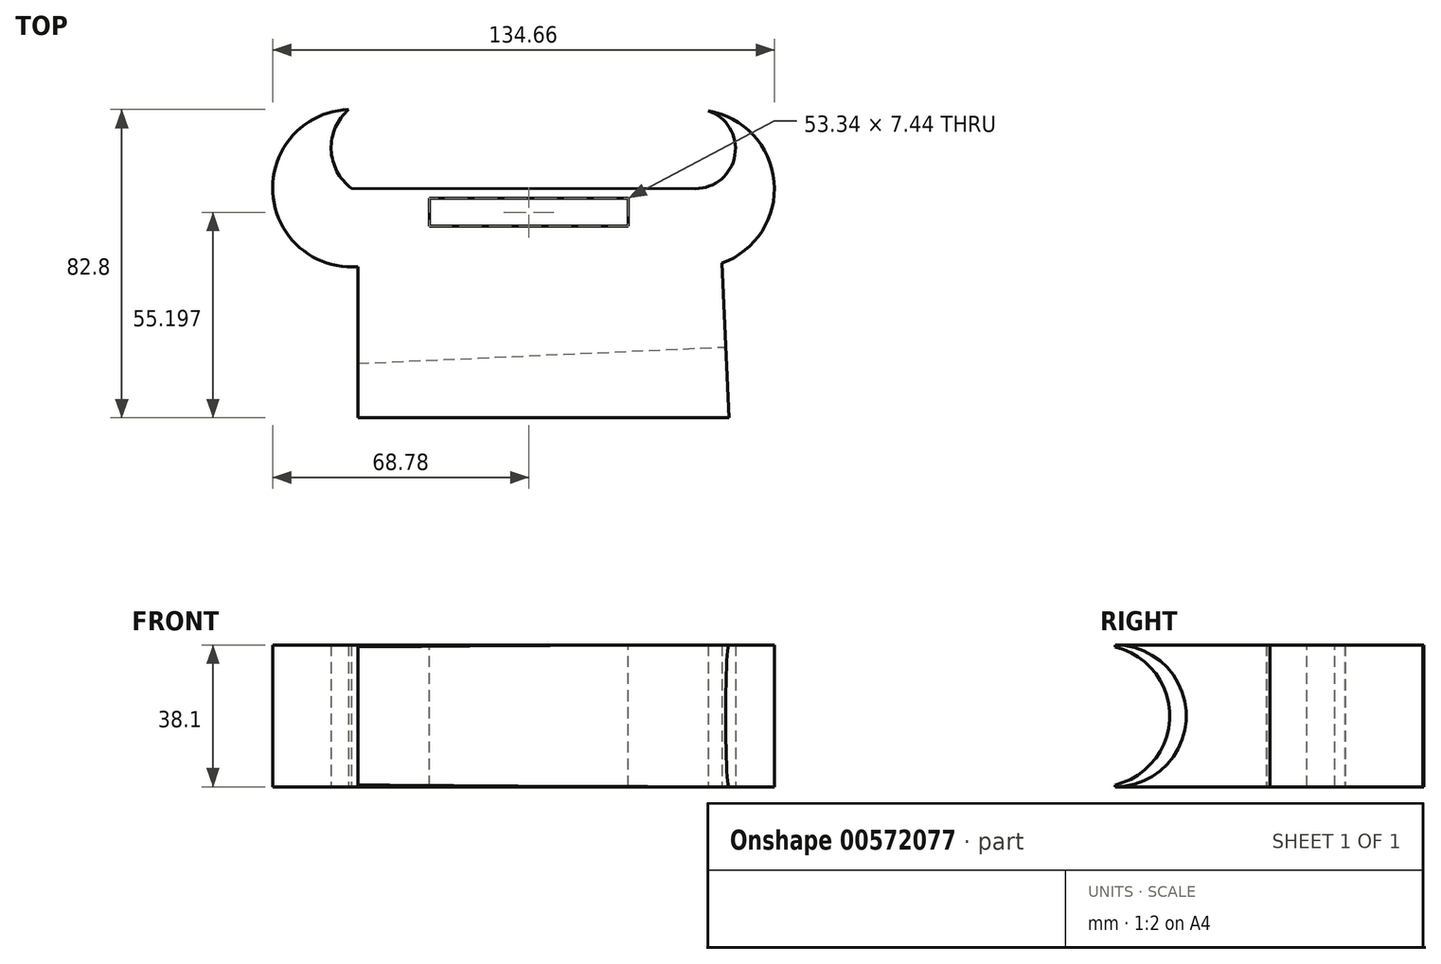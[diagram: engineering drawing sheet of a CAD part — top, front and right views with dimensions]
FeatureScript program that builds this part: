
annotation { "Feature Type Name" : "Feature", "Feature Type Description" : "" }
export const myFeature = defineFeature(function(context is Context, id is Id, definition is map)
    precondition{}
    {
        {
            var Q0;
            Q0=qCreatedBy(makeId("Top.planeOp"),FACE);
            var sketch = newSketch(context, id + "F0", { "sketchPlane" : qUnion([Q0])});
            skArc(sketch, "E0", {"start": v(-48.38, 20.78) * mm, "mid": v(-68.74, -1.58) * mm, "end": v(-45.9, -21.4) * mm});
            skArc(sketch, "E1", {"start": v(51.79, -20.47) * mm, "mid": v(65.8, 1.44) * mm, "end": v(48.07, 20.47) * mm});
            skLineSegment(sketch, "E2", {"start": v(-45.9, -21.4) * mm, "end": v(-45.9, -62.02) * mm});
            skLineSegment(sketch, "E3", {"start": v(-45.9, -62.02) * mm, "end": v(53.65, -62.02) * mm});
            skLineSegment(sketch, "E4", {"start": v(53.65, -62.02) * mm, "end": v(51.79, -20.47) * mm});
            skLineSegment(sketch, "E5", {"start": v(-47.65, -0.34) * mm, "end": v(44.66, -0.48) * mm});
            skArc(sketch, "E6", {"start": v(-48.38, 20.78) * mm, "mid": v(-53.05, 10.04) * mm, "end": v(-47.65, -0.34) * mm});
            skArc(sketch, "E7", {"start": v(44.66, -0.48) * mm, "mid": v(55.29, 8.54) * mm, "end": v(48.07, 20.47) * mm});
            skSolve(sketch);
        }
        {
            var Q0;
            Q0 = qSketchRegion(id + "F0", true);
            extrude(context, id + "F1", {"entities" : qUnion([Q0]), "depth" : 38.1 * mm, "offsetDistance" : 25.4 * mm});
        }
        {
            var Q0;
            Q0=makeQuery(id+"F1.opExtrude","SWEPT_FACE",FACE,{"disambiguationData":[OSD([sQuery(id+"F0.wireOp",EDGE,"E4")])]});
            var sketch = newSketch(context, id + "F2", { "sketchPlane" : qUnion([Q0])});
            skArc(sketch, "E8", {"start": v(-64.36, 0) * mm, "mid": v(-45.31, 19.05) * mm, "end": v(-64.36, 38.1) * mm});
            skSolve(sketch);
        }
        {
            var Q0;
            Q0=makeQuery(id+"F2.imprint","IMPRINT",FACE,{"disambiguationData":[TD([[makeQuery(id+"F2.imprint","IMPRINT",EDGE,{"derivedFrom":sQuery(id+"F2.wireOp",EDGE,"E8")}),1.0]])]});
            extrude(context, id + "F3", {"entities" : qUnion([Q0]), "operationType" : NewBodyOperationType.REMOVE, "oppositeDirection" : true, "depth" : 152.4 * mm, "offsetDistance" : 25.4 * mm});
        }
        {
            var Q0;
            Q0=makeQuery(id+"F1.opExtrude","CAP_FACE",FACE,{"disambiguationData":[OSD([sQuery(id+"F0.wireOp",EDGE,"E0"),sQuery(id+"F0.wireOp",EDGE,"E1"),sQuery(id+"F0.wireOp",EDGE,"E2"),sQuery(id+"F0.wireOp",EDGE,"E3"),sQuery(id+"F0.wireOp",EDGE,"E4"),sQuery(id+"F0.wireOp",EDGE,"E5"),sQuery(id+"F0.wireOp",EDGE,"E6"),sQuery(id+"F0.wireOp",EDGE,"E7")])],"isStart":false});
            var sketch = newSketch(context, id + "F4", { "sketchPlane" : qUnion([Q0])});
            skLineSegment(sketch, "E9.bottom", {"start": v(26.67, -10.54) * mm, "end": v(-26.67, -10.54) * mm});
            skLineSegment(sketch, "E9.top", {"start": v(26.67, -3.1) * mm, "end": v(-26.67, -3.1) * mm});
            skLineSegment(sketch, "E9.left", {"start": v(26.67, -10.54) * mm, "end": v(26.67, -3.1) * mm});
            skLineSegment(sketch, "E9.right", {"start": v(-26.67, -10.54) * mm, "end": v(-26.67, -3.1) * mm});
            skPoint(sketch, "E9.middle", {"position": v(0, -6.82) * mm});
            skSolve(sketch);
        }
        {
            var Q0;
            Q0 = qSketchRegion(id + "F4", true);
            extrude(context, id + "F5", {"entities" : qUnion([Q0]), "operationType" : NewBodyOperationType.REMOVE, "oppositeDirection" : true, "depth" : 152.4 * mm, "offsetDistance" : 25.4 * mm});
        }
    });
